# Revit family: KEUCO_59916000075_
name_source: partatom
category: Generic Models
revit_build: Autodesk Revit 2016 (Build: 20150220_1215(x64)
units: mm (PartAtom-declared; Revit-internal decimal feet)

## family parameters
Always vertical = No
Can host rebar = No
Cut with Voids When Loaded = No
Part Type = Normal
Room Calculation Point = No
Round Connector Dimension = Use Diameter
Shared = No
Work Plane-Based = Yes

## types (1)
- 59916000075
    Artikelnummer = 59916000075
    Ausschreibungstext = KEUCO Grundkörper für Einhebel-Waschtischmischer, 59916000075
für KEUCO Einhebel-Waschtischmischer UP, 

Passend zu Artikel Nr. 
59516010101, 59516011101, 59516012101
59516010102, 59516011102, 59516012102
52916010101, 52916010000, 52916070101
52916070000, 52916170101, 52916170000
    Breite = 45 mm  [stored 0.147638 ft]
    Default Elevation = 1219 mm
    Description = Grundkörper für Wandeinbau,
Einbautiefe 70 - 100 mm
    Gewicht = 0
    Kategorie = ARM
ARM
ARM
    Manufacturer = KEUCO
    Material = Stahl, verchromt
    Serie = Plan
    URL = https://www.keuco.com
    Verwendung = GWC / WP / ZU

note: [stored X ft] marks values corroborated as IEEE doubles in the binary element streams (Revit-internal decimal feet)

## geometry (parser evidence)
native form markers: Sweep x3
no freeform markers — native parametric forms only
